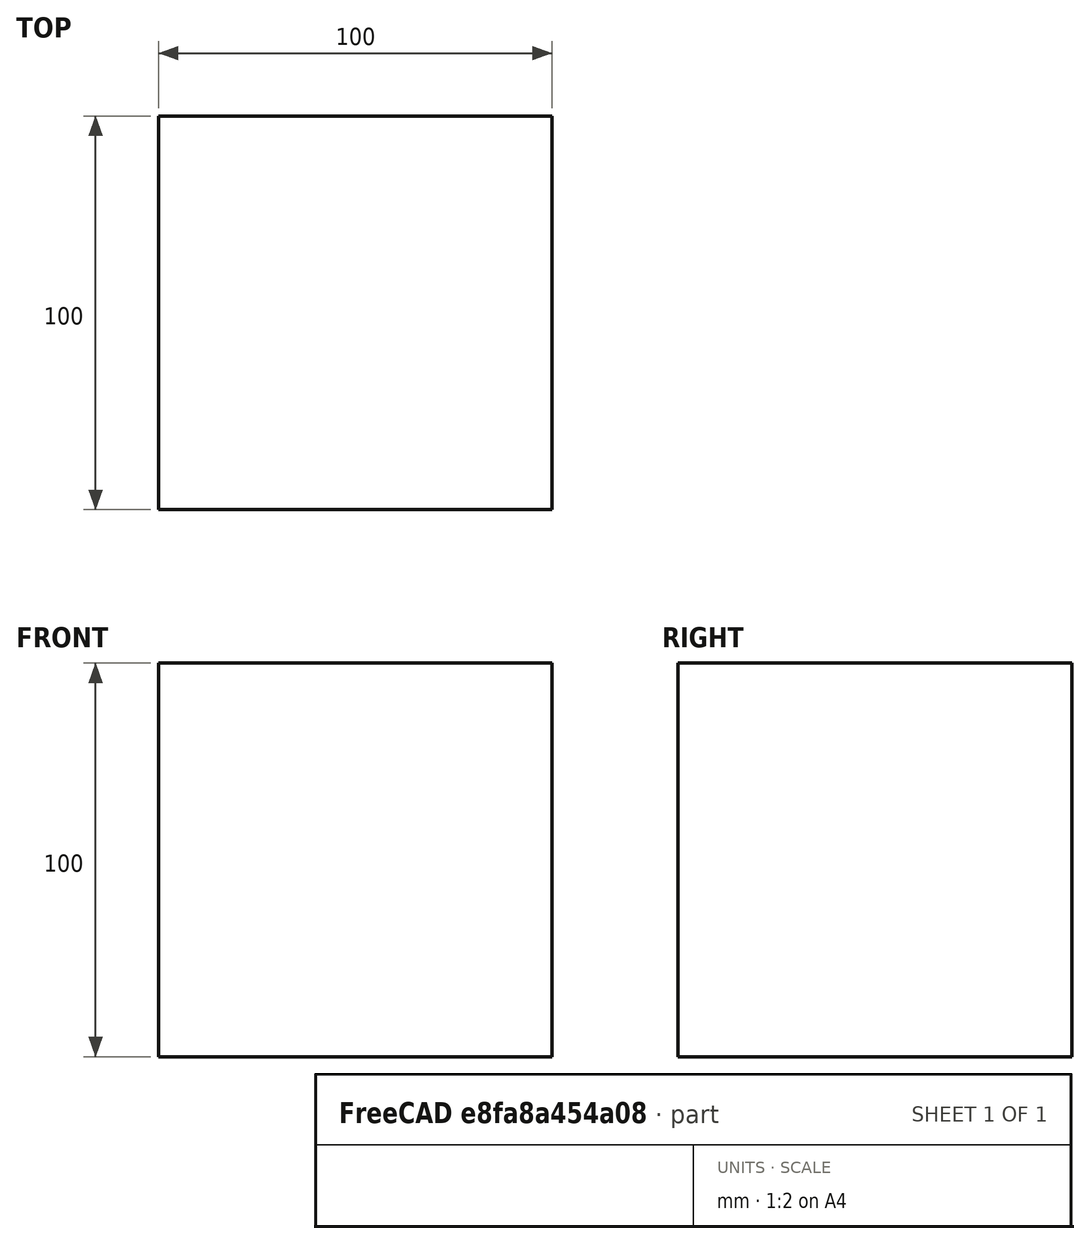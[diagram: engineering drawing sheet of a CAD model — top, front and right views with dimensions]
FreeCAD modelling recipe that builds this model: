
FCSTD DOCUMENT  (FreeCAD 0.19R23074 (Git))
Label: cube3D
License: All rights reserved
LicenseURL: http://en.wikipedia.org/wiki/All_rights_reserved
objects: TechDraw::DrawViewPart×2, TechDraw::DrawViewDimension×2, Sketcher::SketchObject×1, Part::Extrusion×1, TechDraw::DrawSVGTemplate×1, TechDraw::DrawPage×1
note: 2 computed .brp shape members not serialized (recipe doc carries the construction recipe); baked Part::Feature solids carry a one-line shape summary decoded from their .brp

FEATURE [Sketcher::SketchObject] Sketch
  sketch-geometry (4):
    g0: LineSegment StartX=-50 StartY=50 StartZ=0 EndX=50 EndY=50 EndZ=0
    g1: LineSegment StartX=50 StartY=50 StartZ=0 EndX=50 EndY=-50 EndZ=0
    g2: LineSegment StartX=50 StartY=-50 StartZ=0 EndX=-50 EndY=-50 EndZ=0
    g3: LineSegment StartX=-50 StartY=-50 StartZ=0 EndX=-50 EndY=50 EndZ=0
  constraints (10):
    c: Coincident(g0,g1)
    c: Coincident(g1,g2)
    c: Coincident(g2,g3)
    c: Coincident(g3,g0)
    c: Horizontal(g0)
    c: Vertical(g1)
    c: Symmetric(g2,g1,g-2)
    c: Symmetric(g2,g0,g-1)
    c: DistanceX(g2,g2) = 100
    c: DistanceY(g3,g3) = 100
FEATURE [Part::Extrusion] Extrude
  Base = -> Sketch
  Dir = (0,0,1)
  DirMode = 2
  FaceMakerClass = Part::FaceMakerBullseye
  LengthFwd = 100
  LengthRev = 0
  Solid = true
  Symmetric = false
FEATURE [TechDraw::DrawSVGTemplate] Template
  EditableTexts = Designed_by_Name=TEC ET ART; Drawing_number=1; FC-Date=18/12/2020; FC-SC=1; FC-SH=1/1; FC-Title=Cube; Subtitle=Cube
  Height = 210
  Orientation = 1
  Width = 297
FEATURE [TechDraw::DrawViewPart] View
  CoarseView = false
  Direction = (0.577,-0.577,0.577)
  Focus = 100
  HardHidden = false
  IsoCount = 0
  IsoHidden = false
  IsoVisible = false
  LockPosition = false
  Perspective = false
  Rotation = 0
  Scale = 0.4
  ScaleType = 0
  SeamHidden = false
  SeamVisible = true
  SmoothHidden = false
  SmoothVisible = true
  Source = -> [Extrude]
  X = 235.664
  XDirection = (0.707,0.707,0)
  Y = 135.164
FEATURE [TechDraw::DrawViewPart] View001
  CoarseView = false
  Direction = (0,-1,0)
  Focus = 100
  HardHidden = false
  IsoCount = 0
  IsoHidden = false
  IsoVisible = false
  LockPosition = false
  Perspective = false
  Rotation = 0
  ScaleType = 0
  SeamHidden = false
  SeamVisible = true
  SmoothHidden = false
  SmoothVisible = true
  Source = -> [Extrude]
  X = 87.9617
  XDirection = (1,0,0)
  Y = 138.409
FEATURE [TechDraw::DrawViewDimension] Dimension
  Arbitrary = false
  FormatSpec = %.2f
  Inverted = false
  LockPosition = false
  MeasureType = 1
  OverTolerance = 0
  References2D = -> [View001]
  Rotation = 0
  ScaleType = 0
  TheoreticalExact = false
  Type = 1
  UnderTolerance = 0
  X = -4.27034
  Y = -66.8301
FEATURE [TechDraw::DrawViewDimension] Dimension001
  Arbitrary = false
  FormatSpec = %.2f
  Inverted = false
  LockPosition = false
  MeasureType = 1
  OverTolerance = 0
  References2D = -> [View001]
  Rotation = 0
  ScaleType = 0
  TheoreticalExact = false
  Type = 2
  UnderTolerance = 0
  X = 67.5837
  Y = -2.76316
FEATURE [TechDraw::DrawPage] Page
  KeepUpdated = true
  NextBalloonIndex = 1
  ProjectionType = 0
  Template = -> Template
  Views = -> [View,View001,Dimension,Dimension001]
